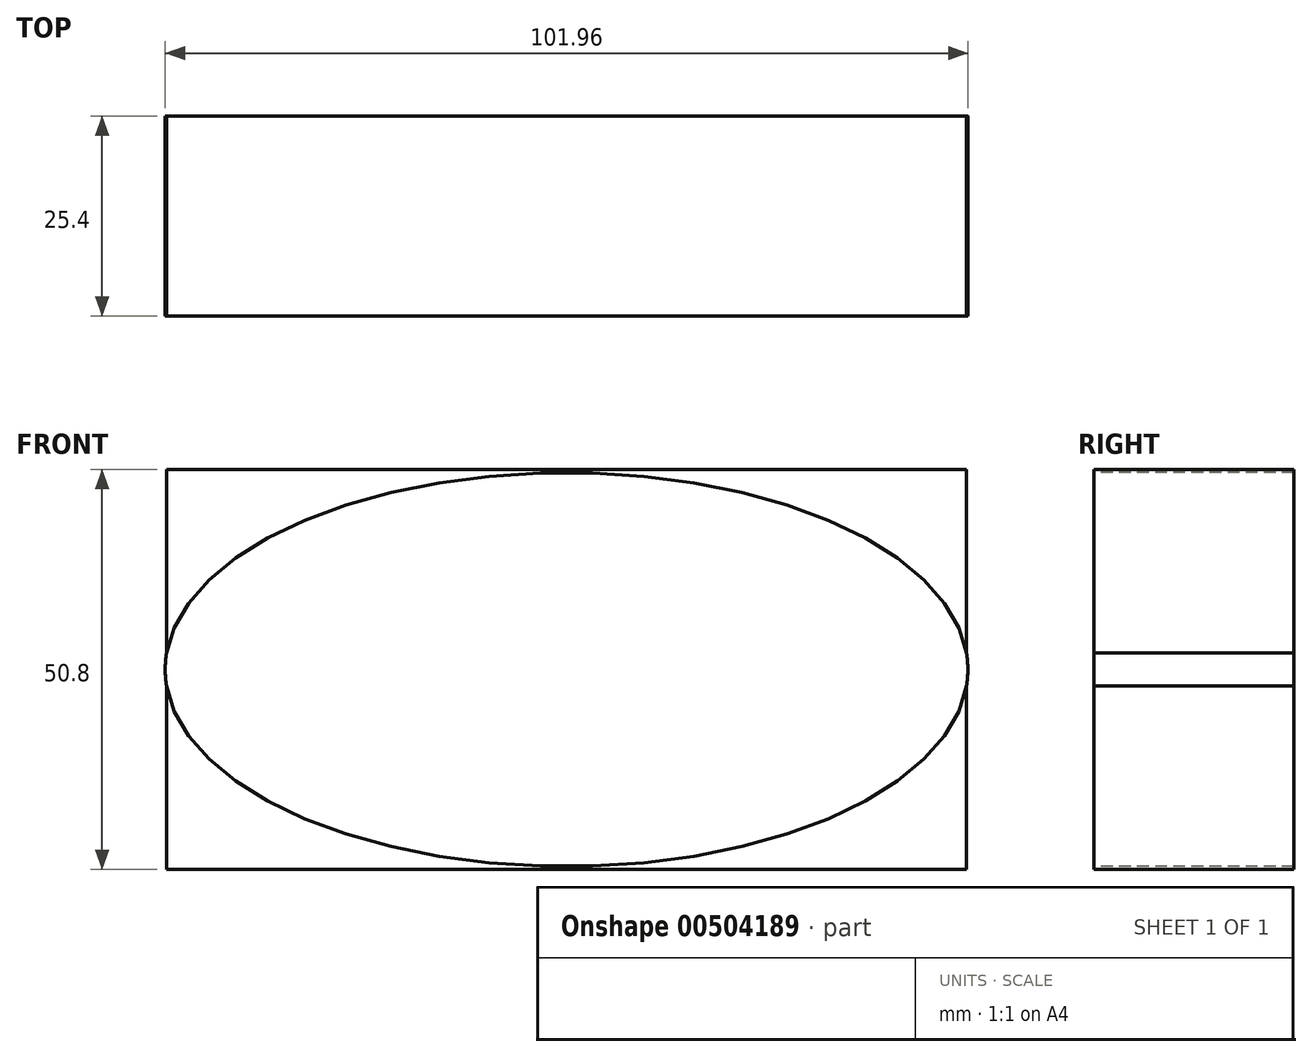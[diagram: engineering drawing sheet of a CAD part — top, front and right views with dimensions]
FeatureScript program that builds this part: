
annotation { "Feature Type Name" : "Feature", "Feature Type Description" : "" }
export const myFeature = defineFeature(function(context is Context, id is Id, definition is map)
    precondition{}
    {
        {
            var Q0;
            Q0=qCreatedBy(makeId("Front.planeOp"),FACE);
            var sketch = newSketch(context, id + "F0", { "sketchPlane" : qUnion([Q0])});
            skLineSegment(sketch, "E0.bottom", {"start": v(-50.8, 25.4) * mm, "end": v(50.8, 25.4) * mm});
            skLineSegment(sketch, "E0.top", {"start": v(-50.8, -25.4) * mm, "end": v(50.8, -25.4) * mm});
            skLineSegment(sketch, "E0.left", {"start": v(-50.8, 25.4) * mm, "end": v(-50.8, -25.4) * mm});
            skLineSegment(sketch, "E0.right", {"start": v(50.8, 25.4) * mm, "end": v(50.8, -25.4) * mm});
            skPoint(sketch, "E0.middle", {"position": v(0, 0) * mm});
            skEllipse(sketch, "E1", {"center": v(0, 0) * mm, "majorRadius": 50.98 * mm, "minorRadius": 25.01 * mm, "majorAxis": v(-1, 0)});
            skSolve(sketch);
        }
        {
            var Q0;
            {var subQ0=sQuery(id+"F0.wireOp",EDGE,"E0.bottom");Q0=makeQuery(id+"F0.imprint","IMPRINT",FACE,{"disambiguationData":[TD([[makeQuery(id+"F0.imprint","IMPRINT",EDGE,{"derivedFrom":subQ0}),-1.0]])]});}
            var Q1;
            {var subQ0=sQuery(id+"F0.wireOp",EDGE,"E0.top");Q1=makeQuery(id+"F0.imprint","IMPRINT",FACE,{"disambiguationData":[TD([[makeQuery(id+"F0.imprint","IMPRINT",EDGE,{"derivedFrom":subQ0}),1.0]])]});}
            extrude(context, id + "F1", {"entities" : qUnion([Q0, Q1]), "depth" : 25.4 * mm});
        }
        {
            var Q0;
            Q0 = qSketchRegion(id + "F0", true);
            extrude(context, id + "F2", {"entities" : qUnion([Q0]), "depth" : 25.4 * mm});
        }
    });
